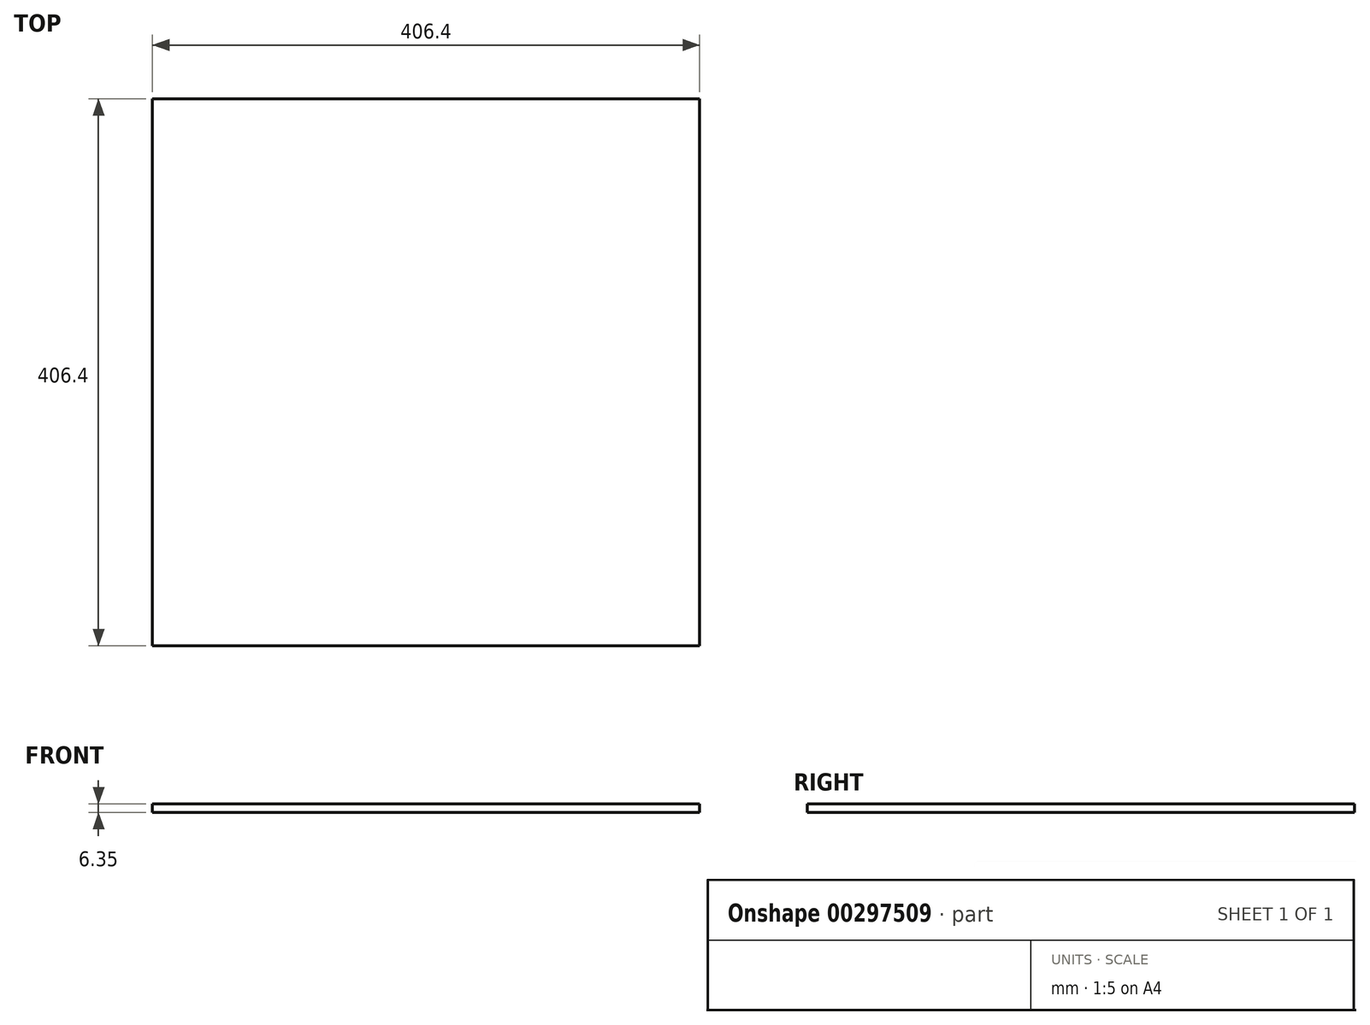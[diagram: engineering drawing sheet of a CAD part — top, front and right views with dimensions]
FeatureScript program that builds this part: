
annotation { "Feature Type Name" : "Feature", "Feature Type Description" : "" }
export const myFeature = defineFeature(function(context is Context, id is Id, definition is map)
    precondition{}
    {
        {
            var Q0;
            Q0=qCreatedBy(makeId("Top.planeOp"),FACE);
            var sketch = newSketch(context, id + "F0", { "sketchPlane" : qUnion([Q0])});
            skLineSegment(sketch, "E0.bottom", {"start": v(0, 0) * mm, "end": v(406.4, 0) * mm});
            skLineSegment(sketch, "E0.top", {"start": v(0, 406.4) * mm, "end": v(406.4, 406.4) * mm});
            skLineSegment(sketch, "E0.left", {"start": v(0, 0) * mm, "end": v(0, 406.4) * mm});
            skLineSegment(sketch, "E0.right", {"start": v(406.4, 0) * mm, "end": v(406.4, 406.4) * mm});
            skSolve(sketch);
        }
        {
            var Q0;
            Q0 = qSketchRegion(id + "F0", true);
            extrude(context, id + "F1", {"entities" : qUnion([Q0]), "depth" : 6.35 * mm});
        }
    });
